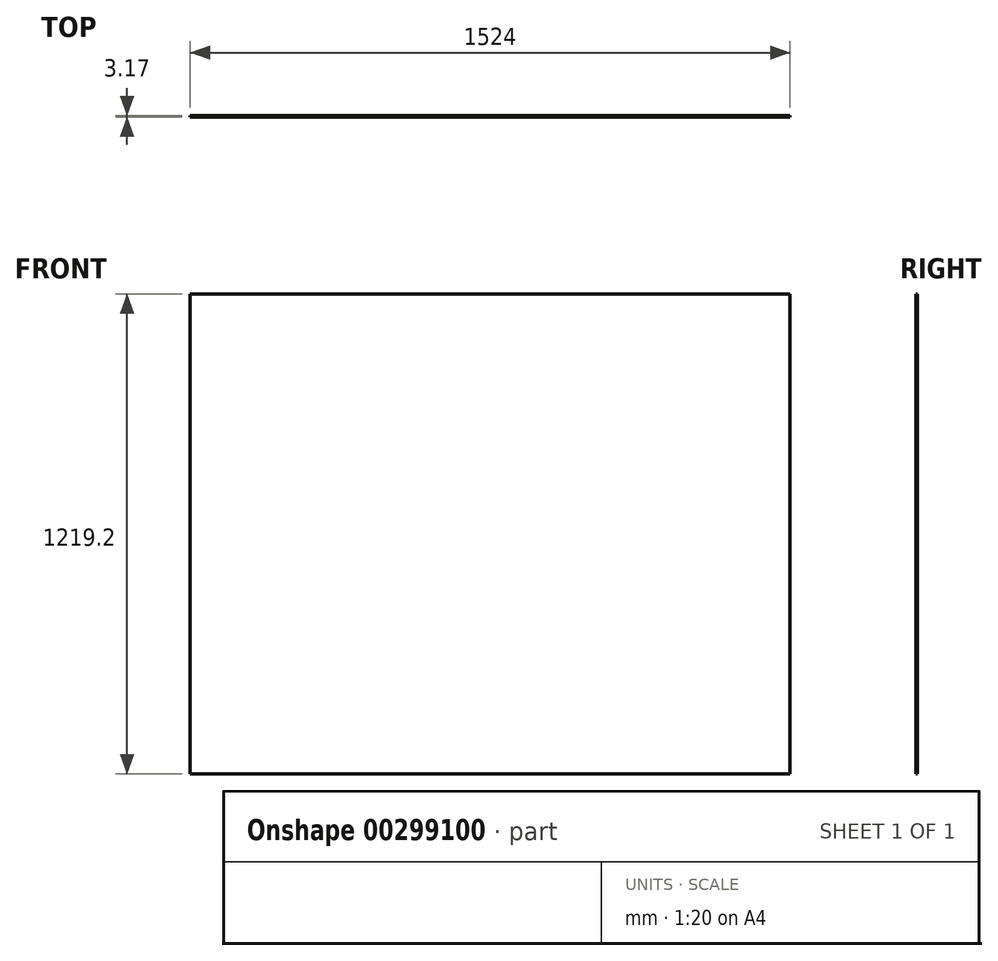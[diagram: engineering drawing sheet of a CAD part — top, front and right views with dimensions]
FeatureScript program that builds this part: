
annotation { "Feature Type Name" : "Feature", "Feature Type Description" : "" }
export const myFeature = defineFeature(function(context is Context, id is Id, definition is map)
    precondition{}
    {
        {
            var Q0;
            Q0=qCreatedBy(makeId("Front.planeOp"),FACE);
            var sketch = newSketch(context, id + "F0", { "sketchPlane" : qUnion([Q0])});
            skLineSegment(sketch, "E0.bottom", {"start": v(-762, 609.6) * mm, "end": v(762, 609.6) * mm});
            skLineSegment(sketch, "E0.top", {"start": v(-762, -609.6) * mm, "end": v(762, -609.6) * mm});
            skLineSegment(sketch, "E0.left", {"start": v(-762, 609.6) * mm, "end": v(-762, -609.6) * mm});
            skLineSegment(sketch, "E0.right", {"start": v(762, 609.6) * mm, "end": v(762, -609.6) * mm});
            skPoint(sketch, "E0.middle", {"position": v(0, 0) * mm});
            skSolve(sketch);
        }
        {
            var Q0;
            Q0 = qSketchRegion(id + "F0", true);
            extrude(context, id + "F1", {"entities" : qUnion([Q0]), "depth" : 3.17 * mm});
        }
    });
